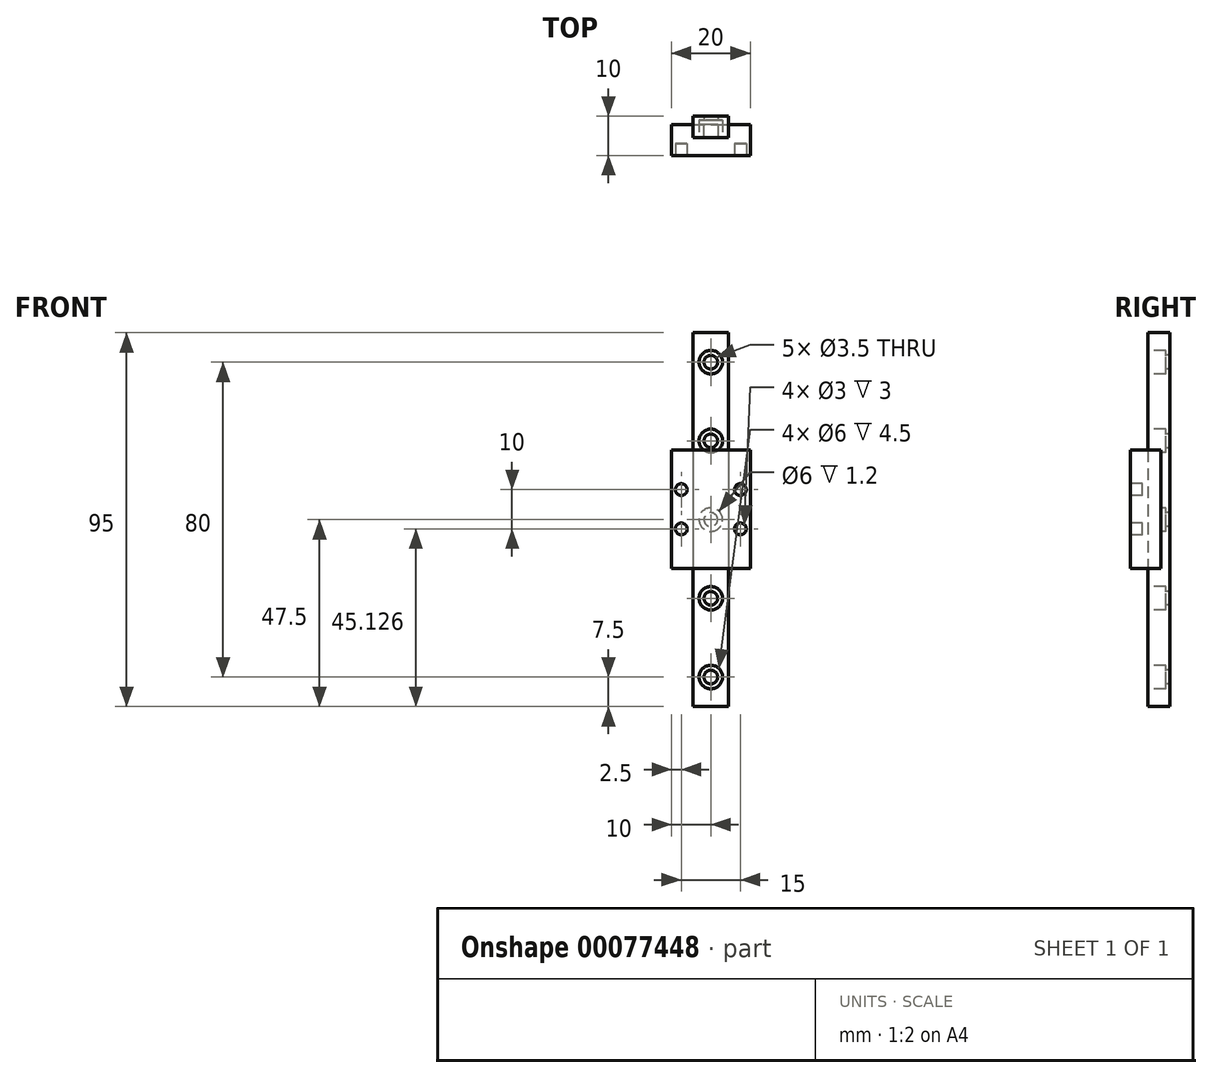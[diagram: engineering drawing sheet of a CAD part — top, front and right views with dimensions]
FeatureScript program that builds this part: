
annotation { "Feature Type Name" : "Feature", "Feature Type Description" : "" }
export const myFeature = defineFeature(function(context is Context, id is Id, definition is map)
    precondition{}
    {
        {
            var Q0;
            Q0=qCreatedBy(makeId("Front.planeOp"),FACE);
            var sketch = newSketch(context, id + "F0", { "sketchPlane" : qUnion([Q0])});
            skLineSegment(sketch, "E0.bottom", {"start": v(-4.5, 47.5) * mm, "end": v(4.5, 47.5) * mm});
            skLineSegment(sketch, "E0.top", {"start": v(-4.5, -47.5) * mm, "end": v(4.5, -47.5) * mm});
            skLineSegment(sketch, "E0.left", {"start": v(-4.5, 47.5) * mm, "end": v(-4.5, -47.5) * mm});
            skLineSegment(sketch, "E0.right", {"start": v(4.5, 47.5) * mm, "end": v(4.5, -47.5) * mm});
            skLineSegment(sketch, "E1", {"start": v(0, 20.52) * mm, "end": v(0, -25.9) * mm, "construction": true});
            skLineSegment(sketch, "E2", {"start": v(-19.4, 0) * mm, "end": v(19.83, 0) * mm, "construction": true});
            skSolve(sketch);
        }
        {
            var Q0;
            Q0=qSketchRegion(id+"F0",true);
            extrude(context, id + "F1", {"entities" : qUnion([Q0]), "depth" : 5.5 * mm});
        }
        {
            var Q0;
            Q0=makeQuery(id+"F1.opExtrude","CAP_FACE",FACE,{"disambiguationData":[OSD([sQuery(id+"F0.wireOp",EDGE,"E0.bottom"),sQuery(id+"F0.wireOp",EDGE,"E0.top"),sQuery(id+"F0.wireOp",EDGE,"E0.left"),sQuery(id+"F0.wireOp",EDGE,"E0.right")])],"isStart":false});
            var sketch = newSketch(context, id + "F2", { "sketchPlane" : qUnion([Q0])});
            skCircle(sketch, "E3", {"center": v(0, 40) * mm, "radius": 1.75 * mm});
            skCircle(sketch, "E4.1.0.0", {"center": v(0, 20) * mm, "radius": 1.75 * mm});
            skCircle(sketch, "E4.2.0.0", {"center": v(0, 0) * mm, "radius": 1.75 * mm});
            skLineSegment(sketch, "E4.direction1", {"start": v(0, 40) * mm, "end": v(0, 20) * mm, "construction": true});
            skCircle(sketch, "E5.0.3.0", {"center": v(0, -20) * mm, "radius": 1.75 * mm});
            skCircle(sketch, "E5.0.4.0", {"center": v(0, -40) * mm, "radius": 1.75 * mm});
            skLineSegment(sketch, "E6", {"start": v(0, 56.3) * mm, "end": v(0, -59.9) * mm, "construction": true});
            skCircle(sketch, "E7", {"center": v(0, 40) * mm, "radius": 3 * mm});
            skCircle(sketch, "E8.1.0.0", {"center": v(0, 20) * mm, "radius": 3 * mm});
            skCircle(sketch, "E8.2.0.0", {"center": v(0, 0) * mm, "radius": 3 * mm});
            skCircle(sketch, "E9.0.3.0", {"center": v(0, -20) * mm, "radius": 3 * mm});
            skCircle(sketch, "E9.0.4.0", {"center": v(0, -40) * mm, "radius": 3 * mm});
            skSolve(sketch);
        }
        {
            var Q0;
            Q0=makeQuery(id+"F2.imprint","IMPRINT",FACE,{"disambiguationData":[TD([[makeQuery(id+"F2.imprint","IMPRINT",EDGE,{"derivedFrom":sQuery(id+"F2.wireOp",EDGE,"E4.1.0.0")}),1.0]])]});
            var Q1;
            Q1=makeQuery(id+"F2.imprint","IMPRINT",FACE,{"disambiguationData":[TD([[makeQuery(id+"F2.imprint","IMPRINT",EDGE,{"derivedFrom":sQuery(id+"F2.wireOp",EDGE,"E3")}),1.0]])]});
            var Q2;
            Q2=makeQuery(id+"F2.imprint","IMPRINT",FACE,{"disambiguationData":[TD([[makeQuery(id+"F2.imprint","IMPRINT",EDGE,{"derivedFrom":sQuery(id+"F2.wireOp",EDGE,"E4.2.0.0")}),1.0]])]});
            var Q3;
            Q3=makeQuery(id+"F2.imprint","IMPRINT",FACE,{"disambiguationData":[TD([[makeQuery(id+"F2.imprint","IMPRINT",EDGE,{"derivedFrom":sQuery(id+"F2.wireOp",EDGE,"E5.0.3.0")}),1.0]])]});
            var Q4;
            Q4=makeQuery(id+"F2.imprint","IMPRINT",FACE,{"disambiguationData":[TD([[makeQuery(id+"F2.imprint","IMPRINT",EDGE,{"derivedFrom":sQuery(id+"F2.wireOp",EDGE,"E5.0.4.0")}),1.0]])]});
            extrude(context, id + "F3", {"entities" : qUnion([Q0, Q1, Q2, Q3, Q4]), "operationType" : NewBodyOperationType.REMOVE, "endBound" : BoundingType.THROUGH_ALL, "oppositeDirection" : true, "depth" : 25 * mm});
        }
        {
            var Q0;
            Q0=qSketchRegion(id+"F2",true);
            extrude(context, id + "F4", {"entities" : qUnion([Q0]), "operationType" : NewBodyOperationType.REMOVE, "oppositeDirection" : true, "depth" : 4.5 * mm});
        }
        {
            var Q0;
            Q0=qCreatedBy(makeId("Front.planeOp"),FACE);
            cPlane(context, id + "F5", {"entities" : qUnion([Q0]), "cplaneType" : CPlaneType.OFFSET, "offset" : 2.2 * mm, "width" : 150 * mm, "height" : 150 * mm});
        }
        {
            var Q0;
            Q0=qCreatedBy(id+"F5.planeOp",FACE);
            var sketch = newSketch(context, id + "F6", { "sketchPlane" : qUnion([Q0])});
            skLineSegment(sketch, "E10.bottom", {"start": v(-10, 17.63) * mm, "end": v(10, 17.63) * mm});
            skLineSegment(sketch, "E10.top", {"start": v(-10, -12.37) * mm, "end": v(10, -12.37) * mm});
            skLineSegment(sketch, "E10.left", {"start": v(-10, 17.63) * mm, "end": v(-10, -12.37) * mm});
            skLineSegment(sketch, "E10.right", {"start": v(10, 17.63) * mm, "end": v(10, -12.37) * mm});
            skSolve(sketch);
        }
        {
            var Q0;
            Q0=makeQuery(id+"F6.imprint","IMPRINT",FACE,{"disambiguationData":[TD([[makeQuery(id+"F6.imprint","IMPRINT",EDGE,{"derivedFrom":sQuery(id+"F6.wireOp",EDGE,"E10.bottom")}),-1.0]])]});
            var Q1;
            Q1=sQuery(id+"F6.wireOp",EDGE,"E10.bottom");
            extrude(context, id + "F7", {"entities" : qUnion([Q0]), "surfaceEntities" : qUnion([Q1]), "depth" : 7.8 * mm});
        }
        {
            var Q0;
            Q0=makeQuery(id+"F7.opExtrude","CAP_FACE",FACE,{"disambiguationData":[OSD([sQuery(id+"F6.wireOp",EDGE,"E10.bottom"),sQuery(id+"F6.wireOp",EDGE,"E10.top"),sQuery(id+"F6.wireOp",EDGE,"E10.left"),sQuery(id+"F6.wireOp",EDGE,"E10.right")])],"isStart":true});
            var sketch = newSketch(context, id + "F8", { "sketchPlane" : qUnion([Q0])});
            skLineSegment(sketch, "E11.bottom", {"start": v(-4.5, 17.63) * mm, "end": v(4.5, 17.63) * mm});
            skLineSegment(sketch, "E11.top", {"start": v(-4.5, -12.37) * mm, "end": v(4.5, -12.37) * mm});
            skLineSegment(sketch, "E11.left", {"start": v(-4.5, 17.63) * mm, "end": v(-4.5, -12.37) * mm});
            skLineSegment(sketch, "E11.right", {"start": v(4.5, 17.63) * mm, "end": v(4.5, -12.37) * mm});
            skSolve(sketch);
        }
        {
            var Q0;
            Q0=qSketchRegion(id+"F8",true);
            var Q1;
            Q1=makeQuery(id+"F1.opExtrude","CAP_FACE",FACE,{"disambiguationData":[OSD([sQuery(id+"F0.wireOp",EDGE,"E0.bottom"),sQuery(id+"F0.wireOp",EDGE,"E0.top"),sQuery(id+"F0.wireOp",EDGE,"E0.left"),sQuery(id+"F0.wireOp",EDGE,"E0.right")])],"isStart":false});
            extrude(context, id + "F9", {"entities" : qUnion([Q0]), "operationType" : NewBodyOperationType.REMOVE, "endBound" : BoundingType.UP_TO_SURFACE, "oppositeDirection" : true, "endBoundEntityFace" : qUnion([Q1]), "depth" : 25 * mm});
        }
        {
            var Q0;
            Q0=makeQuery(id+"F7.opExtrude","CAP_FACE",FACE,{"disambiguationData":[OSD([sQuery(id+"F6.wireOp",EDGE,"E10.bottom"),sQuery(id+"F6.wireOp",EDGE,"E10.top"),sQuery(id+"F6.wireOp",EDGE,"E10.left"),sQuery(id+"F6.wireOp",EDGE,"E10.right")])],"isStart":false});
            var sketch = newSketch(context, id + "F10", { "sketchPlane" : qUnion([Q0])});
            skLineSegment(sketch, "E12", {"start": v(0, 32.73) * mm, "end": v(0, -15.6) * mm, "construction": true});
            skLineSegment(sketch, "E13", {"start": v(-21.44, 2.63) * mm, "end": v(23.02, 2.63) * mm, "construction": true});
            skCircle(sketch, "E14", {"center": v(-7.5, 7.63) * mm, "radius": 1.5 * mm});
            skCircle(sketch, "E15.MirrorC", {"center": v(7.5, 7.63) * mm, "radius": 1.5 * mm});
            skCircle(sketch, "E16.MirrorC", {"center": v(7.5, -2.37) * mm, "radius": 1.5 * mm});
            skCircle(sketch, "E17.MirrorC", {"center": v(-7.5, -2.37) * mm, "radius": 1.5 * mm});
            skSolve(sketch);
        }
        {
            var Q0;
            Q0=qSketchRegion(id+"F10",true);
            extrude(context, id + "F11", {"entities" : qUnion([Q0]), "operationType" : NewBodyOperationType.REMOVE, "oppositeDirection" : true, "depth" : 3 * mm});
        }
    });
